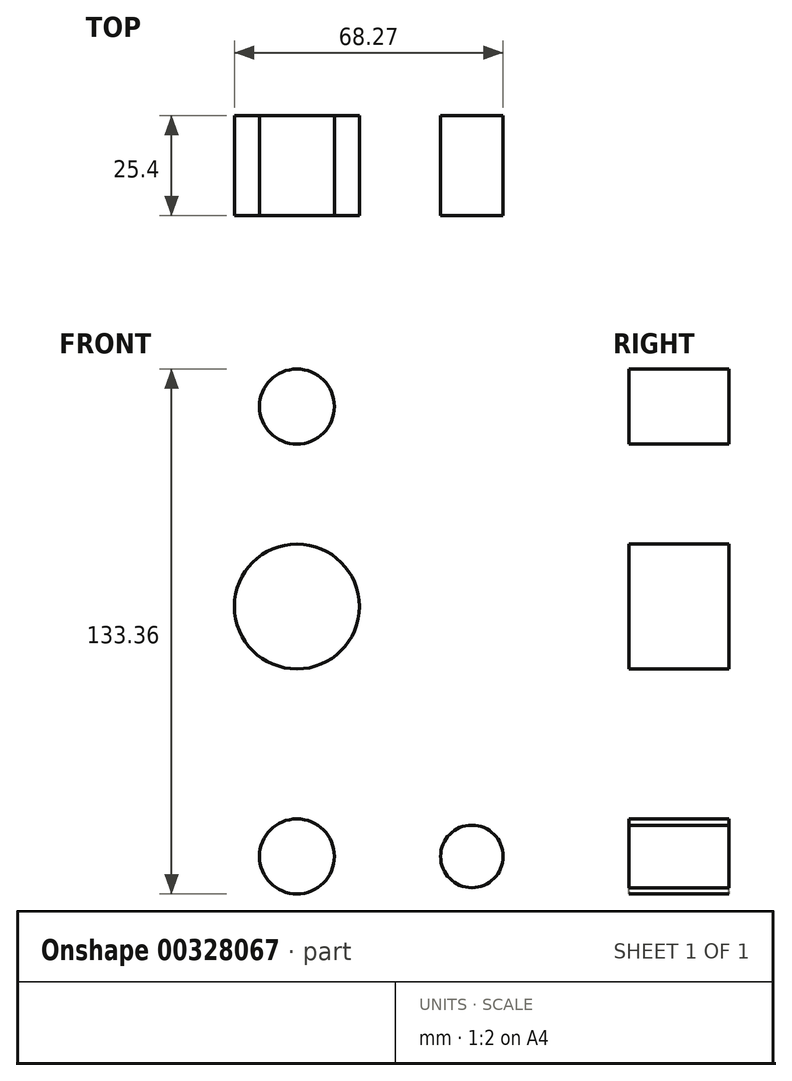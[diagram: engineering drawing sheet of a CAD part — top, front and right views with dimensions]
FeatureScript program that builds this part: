
annotation { "Feature Type Name" : "Feature", "Feature Type Description" : "" }
export const myFeature = defineFeature(function(context is Context, id is Id, definition is map)
    precondition{}
    {
        {
            var Q0;
            Q0=qCreatedBy(makeId("Front.planeOp"),FACE);
            var sketch = newSketch(context, id + "F0", { "sketchPlane" : qUnion([Q0])});
            skLineSegment(sketch, "E0", {"start": v(0, 12.44) * mm, "end": v(0, 12.5) * mm});
            skPoint(sketch, "E1.center.orphan", {"position": v(0, 57.15) * mm});
            skLineSegment(sketch, "E2", {"start": v(0, 12.5) * mm, "end": v(0, 12.44) * mm});
            skPoint(sketch, "E3.end.orphan", {"position": v(-12.46, 0) * mm});
            skPoint(sketch, "E3.start.orphan", {"position": v(-15.73, 61.37) * mm});
            skPoint(sketch, "E4.end.orphan", {"position": v(-15.75, 65.5) * mm});
            skPoint(sketch, "E4.start.orphan", {"position": v(-9.53, 114.3) * mm});
            skPoint(sketch, "E5.center.orphan", {"position": v(0, 114.3) * mm});
            skPoint(sketch, "E5.end.orphan", {"position": v(9.53, 114.3) * mm});
            skPoint(sketch, "E6.end.orphan", {"position": v(15.75, 65.5) * mm});
            skPoint(sketch, "E6.start.orphan", {"position": v(15.73, 61.37) * mm});
            skPoint(sketch, "E7.orphan", {"position": v(44.45, -7.94) * mm});
            skPoint(sketch, "E8.center.orphan", {"position": v(0, 0) * mm});
            skPoint(sketch, "E9.start.orphan", {"position": v(0, -12.44) * mm});
            skPoint(sketch, "E10.start.orphan", {"position": v(44.45, 7.94) * mm});
            skPoint(sketch, "E11.end.orphan", {"position": v(44.45, 0) * mm});
            skLineSegment(sketch, "E12", {"start": v(0, 114.3) * mm, "end": v(0, 0) * mm});
            skLineSegment(sketch, "E13", {"start": v(44.45, 0) * mm, "end": v(0, 0) * mm});
            skCircle(sketch, "E14", {"center": v(0, 114.3) * mm, "radius": 9.53 * mm});
            skCircle(sketch, "E15", {"center": v(0, 63.5) * mm, "radius": 15.88 * mm});
            skCircle(sketch, "E16", {"center": v(44.45, 0) * mm, "radius": 7.94 * mm});
            skCircle(sketch, "E17", {"center": v(0, 0) * mm, "radius": 9.53 * mm});
            skLineSegment(sketch, "E18", {"start": v(0, 63.5) * mm, "end": v(0, 0) * mm});
            skSolve(sketch);
        }
        {
            var Q0;
            Q0 = qSketchRegion(id + "F0", true);
            extrude(context, id + "F1", {"entities" : qUnion([Q0]), "depth" : 25.4 * mm});
        }
        {
            var Q0;
            Q0 = qSketchRegion(id + "F0", true);
            extrude(context, id + "F2", {"entities" : qUnion([Q0]), "depth" : 25.4 * mm});
        }
    });
